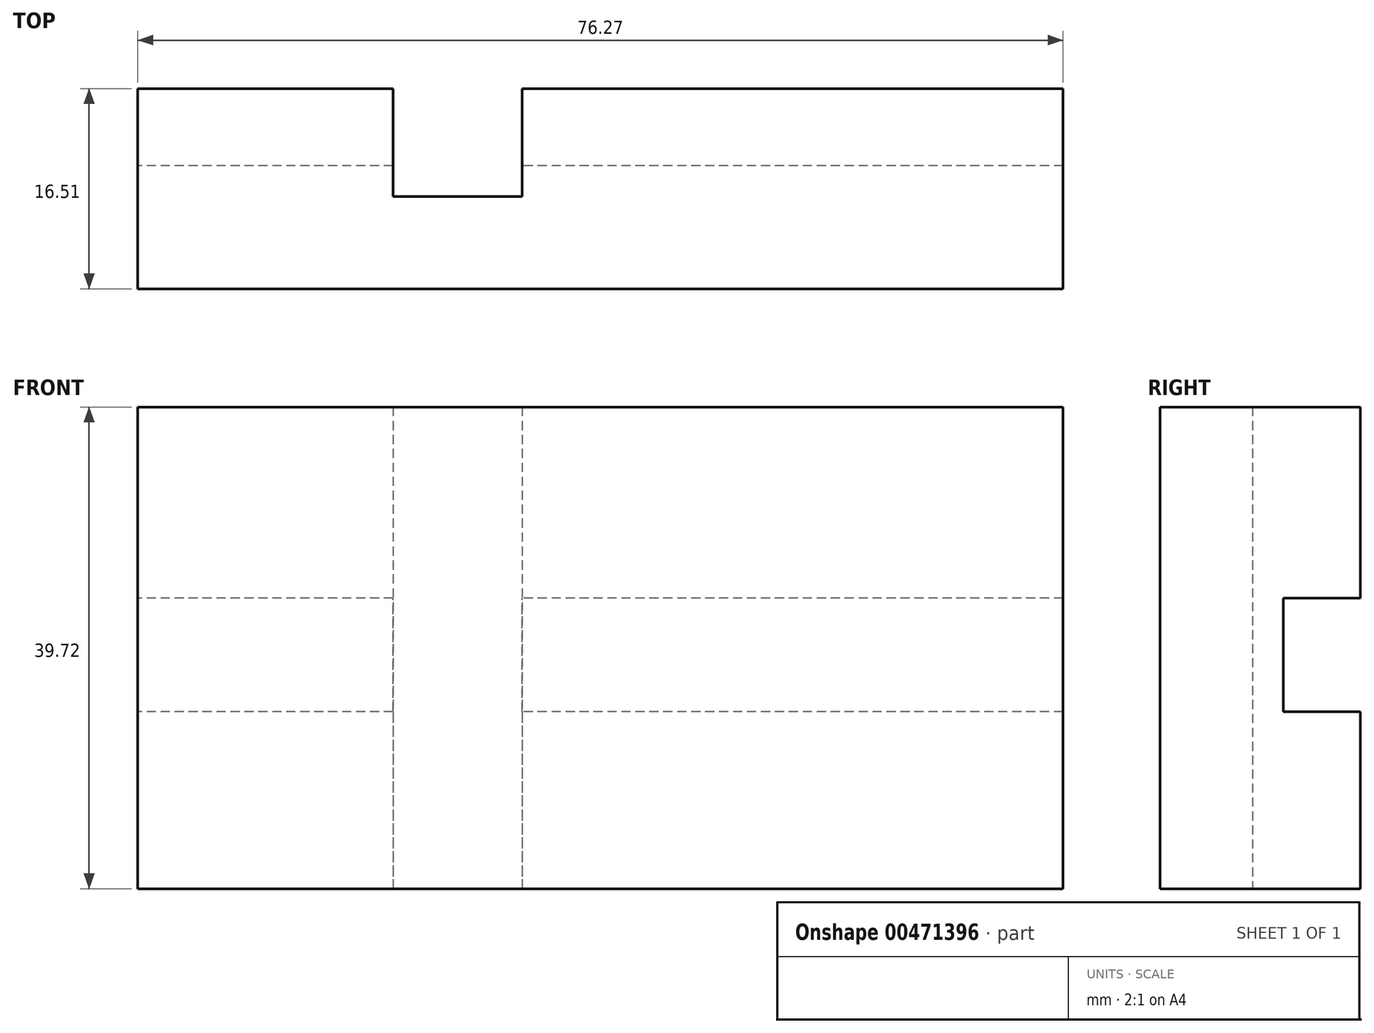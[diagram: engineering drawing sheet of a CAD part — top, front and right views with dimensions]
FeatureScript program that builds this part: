
annotation { "Feature Type Name" : "Feature", "Feature Type Description" : "" }
export const myFeature = defineFeature(function(context is Context, id is Id, definition is map)
    precondition{}
    {
        {
            var Q0;
            Q0=qCreatedBy(makeId("Front.planeOp"),FACE);
            var sketch = newSketch(context, id + "F0", { "sketchPlane" : qUnion([Q0])});
            skLineSegment(sketch, "E0.bottom", {"start": v(0, 0) * mm, "end": v(76.27, 0) * mm});
            skLineSegment(sketch, "E0.top", {"start": v(0, 39.72) * mm, "end": v(76.27, 39.72) * mm});
            skLineSegment(sketch, "E0.left", {"start": v(0, 0) * mm, "end": v(0, 39.72) * mm});
            skLineSegment(sketch, "E0.right", {"start": v(76.27, 0) * mm, "end": v(76.27, 39.72) * mm});
            skSolve(sketch);
        }
        {
            var Q0;
            Q0 = qSketchRegion(id + "F0", true);
            extrude(context, id + "F1", {"entities" : qUnion([Q0]), "depth" : 16.5 * mm});
        }
        {
            var Q0;
            Q0=qCreatedBy(makeId("Front.planeOp"),FACE);
            var sketch = newSketch(context, id + "F2", { "sketchPlane" : qUnion([Q0])});
            skLineSegment(sketch, "E1.bottom", {"start": v(21.04, 39.72) * mm, "end": v(31.7, 39.72) * mm});
            skLineSegment(sketch, "E1.top", {"start": v(21.04, 0) * mm, "end": v(31.7, 0) * mm});
            skLineSegment(sketch, "E1.left", {"start": v(21.04, 39.72) * mm, "end": v(21.04, 0) * mm});
            skLineSegment(sketch, "E1.right", {"start": v(31.7, 39.72) * mm, "end": v(31.7, 0) * mm});
            skLineSegment(sketch, "E2", {"start": v(31.7, 0) * mm, "end": v(21.04, 0) * mm});
            skSolve(sketch);
        }
        {
            var Q0;
            Q0=makeQuery(id+"F2.imprint","IMPRINT",FACE,{"disambiguationData":[TD([[makeQuery(id+"F2.imprint","IMPRINT",EDGE,{"derivedFrom":sQuery(id+"F2.wireOp",EDGE,"E1.bottom")}),-1.0]])]});
            extrude(context, id + "F3", {"entities" : qUnion([Q0]), "operationType" : NewBodyOperationType.REMOVE, "depth" : 8.9 * mm});
        }
        {
            var Q0;
            {var subQ0=sQuery(id+"F0.wireOp",EDGE,"E0.bottom");var subQ1=sQuery(id+"F0.wireOp",EDGE,"E0.right");var subQ2=sQuery(id+"F0.wireOp",EDGE,"E0.top");Q0=makeQuery(id+"F3.boolean.opBoolean","SPLIT",FACE,{"disambiguationData":[TD([makeQuery(id+"F1.opExtrude","SWEPT_FACE",FACE,{"disambiguationData":[OSD([subQ1])]})])],"derivedFrom":makeQuery(id+"F1.opExtrude","CAP_FACE",FACE,{"disambiguationData":[OSD([subQ0,subQ2,sQuery(id+"F0.wireOp",EDGE,"E0.left"),subQ1])],"isStart":true})});}
            var sketch = newSketch(context, id + "F4", { "sketchPlane" : qUnion([Q0])});
            skLineSegment(sketch, "E3.bottom", {"start": v(-76.27, 23.95) * mm, "end": v(0, 23.95) * mm});
            skLineSegment(sketch, "E3.top", {"start": v(-76.27, 14.6) * mm, "end": v(0, 14.6) * mm});
            skLineSegment(sketch, "E3.left", {"start": v(-76.27, 23.95) * mm, "end": v(-76.27, 14.6) * mm});
            skLineSegment(sketch, "E3.right", {"start": v(0, 23.95) * mm, "end": v(0, 14.6) * mm});
            skSolve(sketch);
        }
        {
            var Q0;
            Q0 = qSketchRegion(id + "F4", true);
            extrude(context, id + "F5", {"entities" : qUnion([Q0]), "operationType" : NewBodyOperationType.REMOVE, "oppositeDirection" : true, "depth" : 6.35 * mm});
        }
    });
